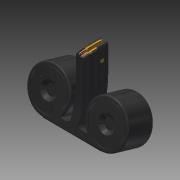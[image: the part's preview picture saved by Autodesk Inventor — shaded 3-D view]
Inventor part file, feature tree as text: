
AUTODESK INVENTOR PART (.ipt)
format: ipt  version: 2013 (Build 170138000, 138)  size: 5,565,952 bytes
history: native  units: in
note: dims shown in document units (in); Inventor stores cm internally (conversion verified against a paired STEP export)
features: extrude x6, sketch x6, fillet x5, other x3, chamfer x2, projected_geometry x1
ambient origin geometry x8: Origin, YZ Plane, XZ Plane, XY Plane, X Axis, Y Axis, Z Axis, Center Point
bodies: Solid1 (feature_tree)
feature tree (23):
  other  "M16_AR-15_M4_ Magazine1"
  extrude  "Extrusion1"  Depth=0.05in TaperAngle=0.0deg
  extrude  "Extrusion2"  Depth=0.125in
  fillet  "Fillet1"  Radius=0.1in
  fillet  "Fillet2"  Radius=0.2in
  extrude  "Extrusion3"  Depth=0.2in TaperAngle=0.0deg
  extrude  "Extrusion4"  Depth=0.125in
  chamfer  "Chamfer1"  Distance=0.2in
  extrude  "Extrusion5"  Depth=0.05in
  chamfer  "Chamfer2"  [1 undecoded]
  fillet  "Fillet3"  [1 undecoded]
  extrude  "Extrusion6"  [1 undecoded]
  fillet  "Fillet4"  [1 undecoded]
  fillet  "Fillet5"  [1 undecoded]
  sketch  "Sketch1"  dims[d0=1.0in d1=0.0in d2=0.05in d3=0.0in]
  sketch  "Sketch2"  dims[d4=0.125in d5=0.125in d6=0.1in d7=0.0in d8=0.2in d9=0.0in]
  sketch  "Sketch3"  dims[d10=0.3in d11=0.125in d12=45.0deg d13=0.2in d14=0.0in]
  sketch  "Sketch4"  dims[d15=0.2in d16=0.125in d17=45.0deg d18=0.125in d19=0.2in d20=0.0in]
  projected_geometry  "Projected Loop1"
  sketch  "Sketch5"  dims[d21=0.05in d22=0.05in]
  sketch  "Sketch6"
  other  "Composite1"
  other  "Srf1"
note: 5 required parameter values undecoded (feature->parameter linkage not recoverable at this tier; creation-order binding heuristic only, values carry confidence <= 0.55)
